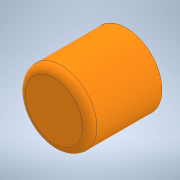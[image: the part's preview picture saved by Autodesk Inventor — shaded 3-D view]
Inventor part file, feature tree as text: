
AUTODESK INVENTOR PART (.ipt)
format: ipt  version: 2022.1 (Build 261234000, 234)  size: 117,248 bytes
history: native  units: in
note: dims shown in document units (in); Inventor stores cm internally (conversion verified against a paired STEP export)
features: extrude x1, fillet x1, sketch x1
ambient origin geometry x8: Origin, YZ Plane, XZ Plane, XY Plane, X Axis, Y Axis, Z Axis, Center Point
bodies: Solid1 (feature_tree)
feature tree (3):
  extrude  "Extrusion1"  Depth=0.1986in TaperAngle=0.0deg
  fillet  "Face Fillet1"
  sketch  "Sketch1"  dims[d0=0.1969in d1=0.1986in d2=0.0in d3=0.02in]
